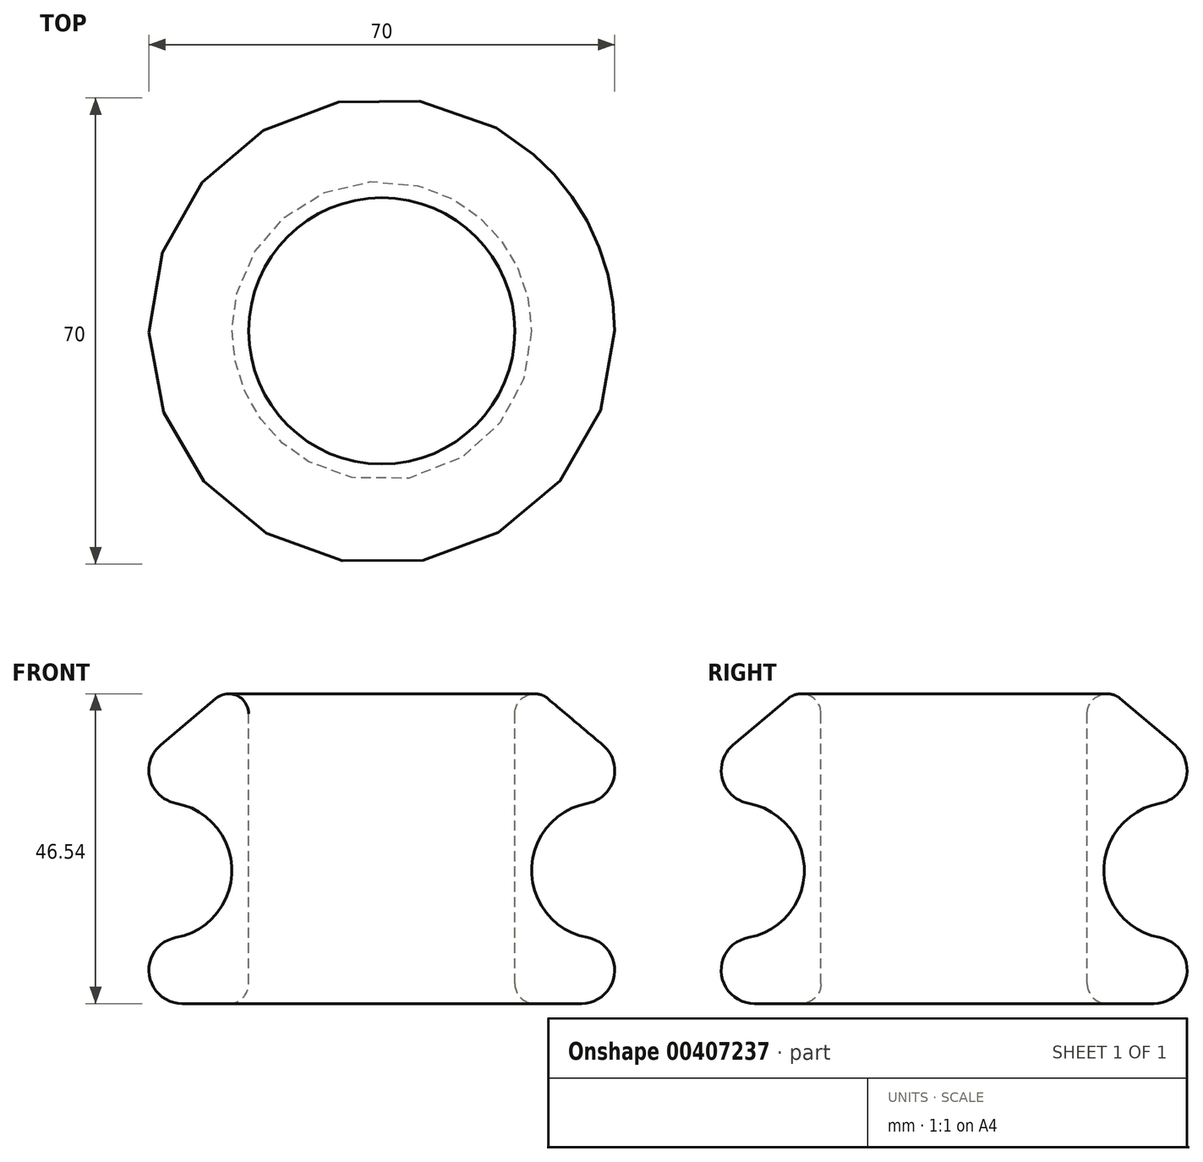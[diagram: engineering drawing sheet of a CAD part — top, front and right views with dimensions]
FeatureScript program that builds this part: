
annotation { "Feature Type Name" : "Feature", "Feature Type Description" : "" }
export const myFeature = defineFeature(function(context is Context, id is Id, definition is map)
    precondition{}
    {
        {
            var Q0;
            Q0=qCreatedBy(makeId("Front.planeOp"),FACE);
            var sketch = newSketch(context, id + "F0", { "sketchPlane" : qUnion([Q0])});
            skArc(sketch, "E0", {"start": v(-30, 20) * mm, "mid": v(-34.98, 15.45) * mm, "end": v(-30.9, 10.08) * mm});
            skLineSegment(sketch, "E1", {"start": v(0, 56.78) * mm, "end": v(0, -59.13) * mm, "construction": true});
            skArc(sketch, "E2", {"start": v(-22.5, 0) * mm, "mid": v(-24.88, 6.56) * mm, "end": v(-30.9, 10.08) * mm});
            skPoint(sketch, "E3", {"position": v(-22.5, 0) * mm});
            skLineSegment(sketch, "E4.bottom", {"start": v(-30, 20) * mm, "end": v(-20, 20) * mm});
            skLineSegment(sketch, "E5", {"start": v(-71.62, 0) * mm, "end": v(26.31, 0) * mm, "construction": true});
            skLineSegment(sketch, "E6", {"start": v(-20, 20) * mm, "end": v(-20, 0) * mm});
            skPoint(sketch, "E6.endSnap0", {"position": v(-22.65, 0) * mm});
            skArc(sketch, "E7.MirrorCS", {"start": v(-22.5, 0) * mm, "mid": v(-24.88, -6.56) * mm, "end": v(-30.9, -10.08) * mm});
            skArc(sketch, "E8.MirrorCS", {"start": v(-30, -20) * mm, "mid": v(-34.98, -15.45) * mm, "end": v(-30.9, -10.08) * mm});
            skLineSegment(sketch, "E9.MirrorCS", {"start": v(-30, -20) * mm, "end": v(-20, -20) * mm});
            skLineSegment(sketch, "E10.MirrorCS", {"start": v(-20, -20) * mm, "end": v(-20, 0) * mm});
            skLineSegment(sketch, "E11", {"start": v(-20, 20) * mm, "end": v(-20, 30) * mm});
            skLineSegment(sketch, "E12", {"start": v(-20, 30) * mm, "end": v(-33.23, 18.82) * mm});
            skSolve(sketch);
        }
        {
            var Q0;
            Q0=qSketchRegion(id+"F0",true);
            var Q1;
            Q1=sQuery(id+"F0.wireOp",EDGE,"E1");
            revolve(context, id + "F1", {"entities" : qUnion([Q0]), "axis" : qUnion([Q1]), "revolveType" : RevolveType.FULL});
        }
        {
            var Q0;
            Q0=makeQuery(id+"F1.opRevolve","SWEPT_EDGE",EDGE,{"disambiguationData":[OSD([sQuery(id+"F0.wireOp",EDGE,"E9.MirrorCS"),sQuery(id+"F0.wireOp",EDGE,"E10.MirrorCS")])]});
            var Q1;
            Q1=makeQuery(id+"F1.opRevolve","SWEPT_EDGE",EDGE,{"disambiguationData":[OSD([sQuery(id+"F0.wireOp",EDGE,"E11"),sQuery(id+"F0.wireOp",EDGE,"E12")])]});
            fillet(context, id + "F2", {"entities" : qUnion([Q0, Q1]), "radius" : 3 * mm, "tangentPropagation" : true, "allowEdgeOverflow" : false});
        }
    });
